# Revit family: Building-FlushMountingEnclosures-GEWISS-24SC-UNDERFLOOR_BOXES
name_source: partatom
category: Apparecchi elettrici
revit_build: Autodesk Revit 2016 (Build: 20161004_0715(x64)
units: mm (PartAtom-declared; Revit-internal decimal feet)

## family parameters
Condiviso = Sì
Host = Superficie
Mantenere orientamento annotazione = Sì
Punto di calcolo locali = Sì
Quota connettore circolare = Usa diametro
Taglio con vuoti quando caricato = Sì
Tipo di parte = Normale

## types (2) — shared parameters
Catalogue = BUILDING
Catalogue Range = 24SC
Electrocod = 200
IDF = 92f5f222-8233-4daf-bba0-a6884685a3f9
IDT = eb2e272e-e186-4efe-a574-cdabb52c6024
Immagine tipo = GW24622.jpg
Material = Metal
Produttore = GEWISS S.p.A.
Prospetto di default = 1219 mm
SEO = Casing
Technical sheet = https://www.gewiss.com
Tipo = Torrette a Scomparsa Casseforme_GENERICO : GW24622 Cassaforma in metallo per torretta 20-32p
URL = https://www.gewiss.com
Version file RFA = 19.0

## per-type parameters (varying)
| type | Descrizione | EAN code | Modello | Suitable for outlet boxes |
| GW24622 - Metal casing for und.outlet box 20-32M | METAL CASING FOR UND.OUTLET BOX 20-32M | 8011564759664 | GW24622 | GW24602, GW24612, GW24607, GW24617 |
| GW24621 - Metal casing for und.outlet box 10-16M | METAL CASING FOR UND.OUTLET BOX 10-16M | 8011564759657 | GW24621 | GW24601, GW24611, GW24606, GW24616 |

## geometry (parser evidence)
native form markers: Blend x2, Sweep x2
no freeform markers — native parametric forms only
